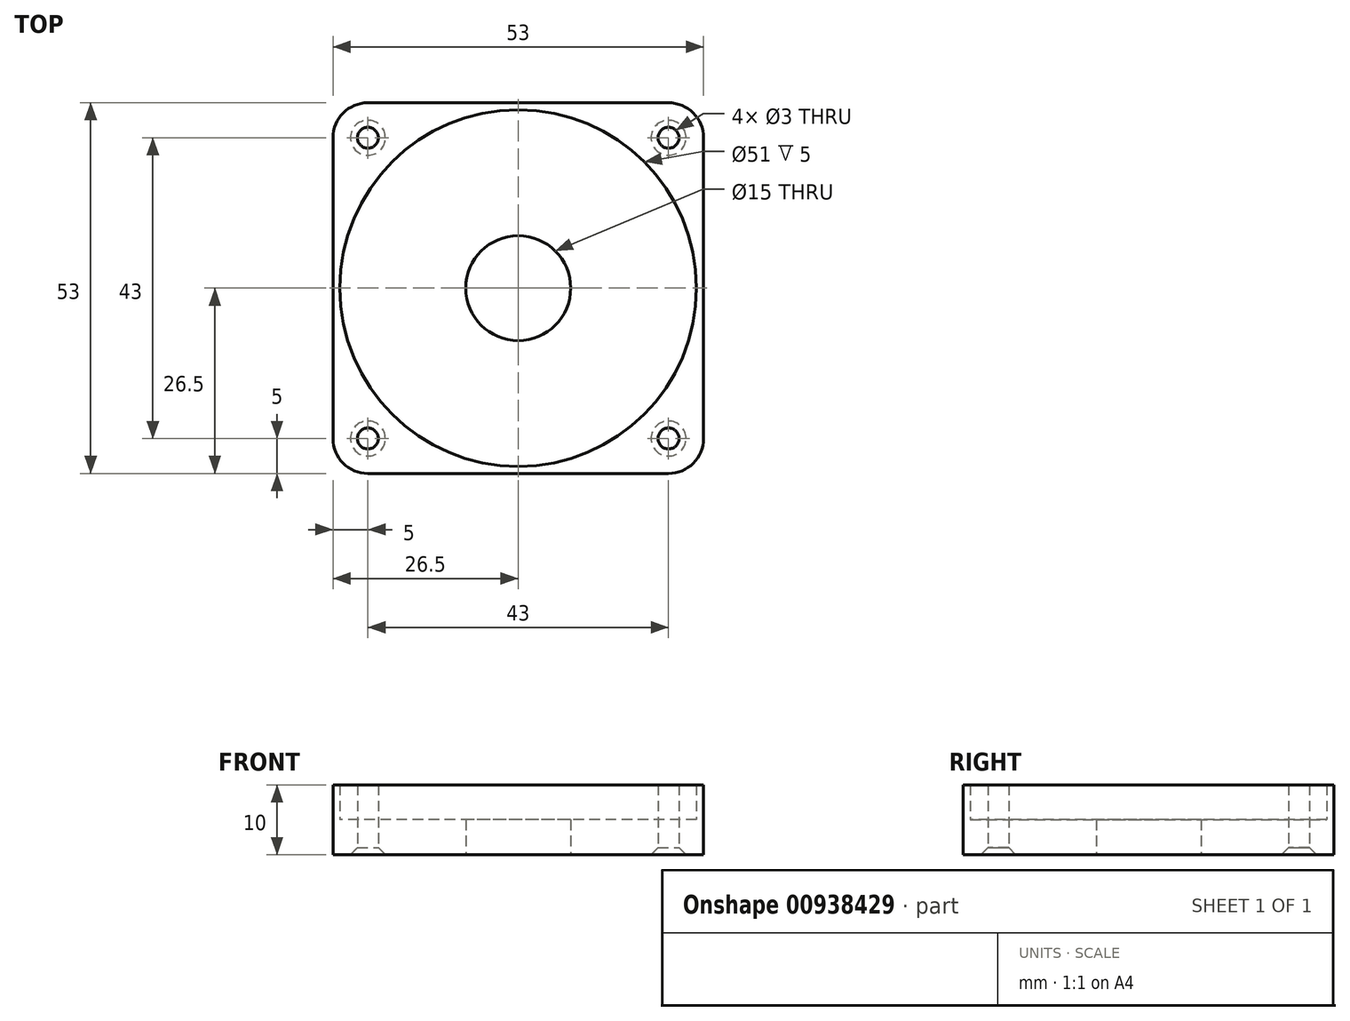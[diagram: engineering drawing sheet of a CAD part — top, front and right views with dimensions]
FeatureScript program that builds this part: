
annotation { "Feature Type Name" : "Feature", "Feature Type Description" : "" }
export const myFeature = defineFeature(function(context is Context, id is Id, definition is map)
    precondition{}
    {
        {
            var Q0;
            Q0=qCreatedBy(makeId("Top.planeOp"),FACE);
            var sketch = newSketch(context, id + "F0", { "sketchPlane" : qUnion([Q0])});
            skLineSegment(sketch, "E0.bottom", {"start": v(-21.5, 26.5) * mm, "end": v(21.5, 26.5) * mm});
            skLineSegment(sketch, "E0.top", {"start": v(-21.5, -26.5) * mm, "end": v(21.5, -26.5) * mm});
            skLineSegment(sketch, "E0.left", {"start": v(-26.5, 21.5) * mm, "end": v(-26.5, -21.5) * mm});
            skLineSegment(sketch, "E0.right", {"start": v(26.5, 21.5) * mm, "end": v(26.5, -21.5) * mm});
            skPoint(sketch, "E0.middle", {"position": v(0, 0) * mm});
            skCircle(sketch, "E1", {"center": v(0, 0) * mm, "radius": 25.5 * mm});
            skCircle(sketch, "E2", {"center": v(0, 0) * mm, "radius": 7.5 * mm});
            skPoint(sketch, "E3.visualSharp", {"position": v(-26.5, 26.5) * mm});
            skArc(sketch, "E3.filletArc", {"start": v(-21.5, 26.5) * mm, "mid": v(-25.04, 25.04) * mm, "end": v(-26.5, 21.5) * mm});
            skPoint(sketch, "E4.visualSharp", {"position": v(26.5, 26.5) * mm});
            skArc(sketch, "E4.filletArc", {"start": v(26.5, 21.5) * mm, "mid": v(25.04, 25.04) * mm, "end": v(21.5, 26.5) * mm});
            skPoint(sketch, "E5.visualSharp", {"position": v(26.5, -26.5) * mm});
            skArc(sketch, "E5.filletArc", {"start": v(21.5, -26.5) * mm, "mid": v(25.04, -25.04) * mm, "end": v(26.5, -21.5) * mm});
            skPoint(sketch, "E6.visualSharp", {"position": v(-26.5, -26.5) * mm});
            skArc(sketch, "E6.filletArc", {"start": v(-26.5, -21.5) * mm, "mid": v(-25.04, -25.04) * mm, "end": v(-21.5, -26.5) * mm});
            skSolve(sketch);
        }
        {
            var Q0;
            Q0=qSketchRegion(id+"F0",true);
            extrude(context, id + "F1", {"entities" : qUnion([Q0]), "depth" : 10 * mm, "offsetDistance" : 25 * mm});
        }
        {
            var Q0;
            Q0=makeQuery(id+"F0.imprint","IMPRINT",FACE,{"disambiguationData":[TD([[makeQuery(id+"F0.imprint","IMPRINT",EDGE,{"derivedFrom":sQuery(id+"F0.wireOp",EDGE,"E1")}),1.0]])]});
            extrude(context, id + "F2", {"entities" : qUnion([Q0]), "operationType" : NewBodyOperationType.ADD, "depth" : 5 * mm, "offsetDistance" : 25 * mm});
        }
        {
            var Q0;
            Q0=qCreatedBy(makeId("Top.planeOp"),FACE);
            var sketch = newSketch(context, id + "F3", { "sketchPlane" : qUnion([Q0])});
            skPoint(sketch, "E7", {"position": v(-21.5, 21.5) * mm});
            skPoint(sketch, "E8", {"position": v(21.5, 21.5) * mm});
            skPoint(sketch, "E9", {"position": v(21.5, -21.5) * mm});
            skPoint(sketch, "E10", {"position": v(-21.5, -21.5) * mm});
            skSolve(sketch);
        }
        {
            var Q0;
            Q0=sQuery(id+"F3.wireOp",VERTEX,"E7");
            var Q1;
            Q1=sQuery(id+"F3.wireOp",VERTEX,"E10");
            var Q2;
            Q2=sQuery(id+"F3.wireOp",VERTEX,"E9");
            var Q3;
            Q3=sQuery(id+"F3.wireOp",VERTEX,"E8");
            var Q4;
            Q4=makeQuery(id+"F1.opExtrude","SWEPT_BODY",BODY,{"disambiguationData":[OSD([sQuery(id+"F0.wireOp",EDGE,"E0.bottom"),sQuery(id+"F0.wireOp",EDGE,"E0.top"),sQuery(id+"F0.wireOp",EDGE,"E0.left"),sQuery(id+"F0.wireOp",EDGE,"E0.right"),sQuery(id+"F0.wireOp",EDGE,"E1"),sQuery(id+"F0.wireOp",EDGE,"E3.filletArc"),sQuery(id+"F0.wireOp",EDGE,"E4.filletArc"),sQuery(id+"F0.wireOp",EDGE,"E5.filletArc"),sQuery(id+"F0.wireOp",EDGE,"E6.filletArc")])]});
            hole(context, id + "F4", {"style" : HoleStyle.C_SINK, "endStyle" : HoleEndStyle.BLIND, "oppositeDirection" : true, "holeDiameter" : 3 * mm, "cSinkDiameter" : 5 * mm, "cSinkAngle" : 90 * degree, "majorDiameter" : 5 * mm, "holeDepth" : 11 * mm, "isTappedThrough" : true, "tappedDepth" : 12 * mm, "tapClearance" : 3, "startFromSketch" : true, "locations" : qUnion([Q0, Q1, Q2, Q3]), "scope" : qUnion([Q4])});
        }
    });
